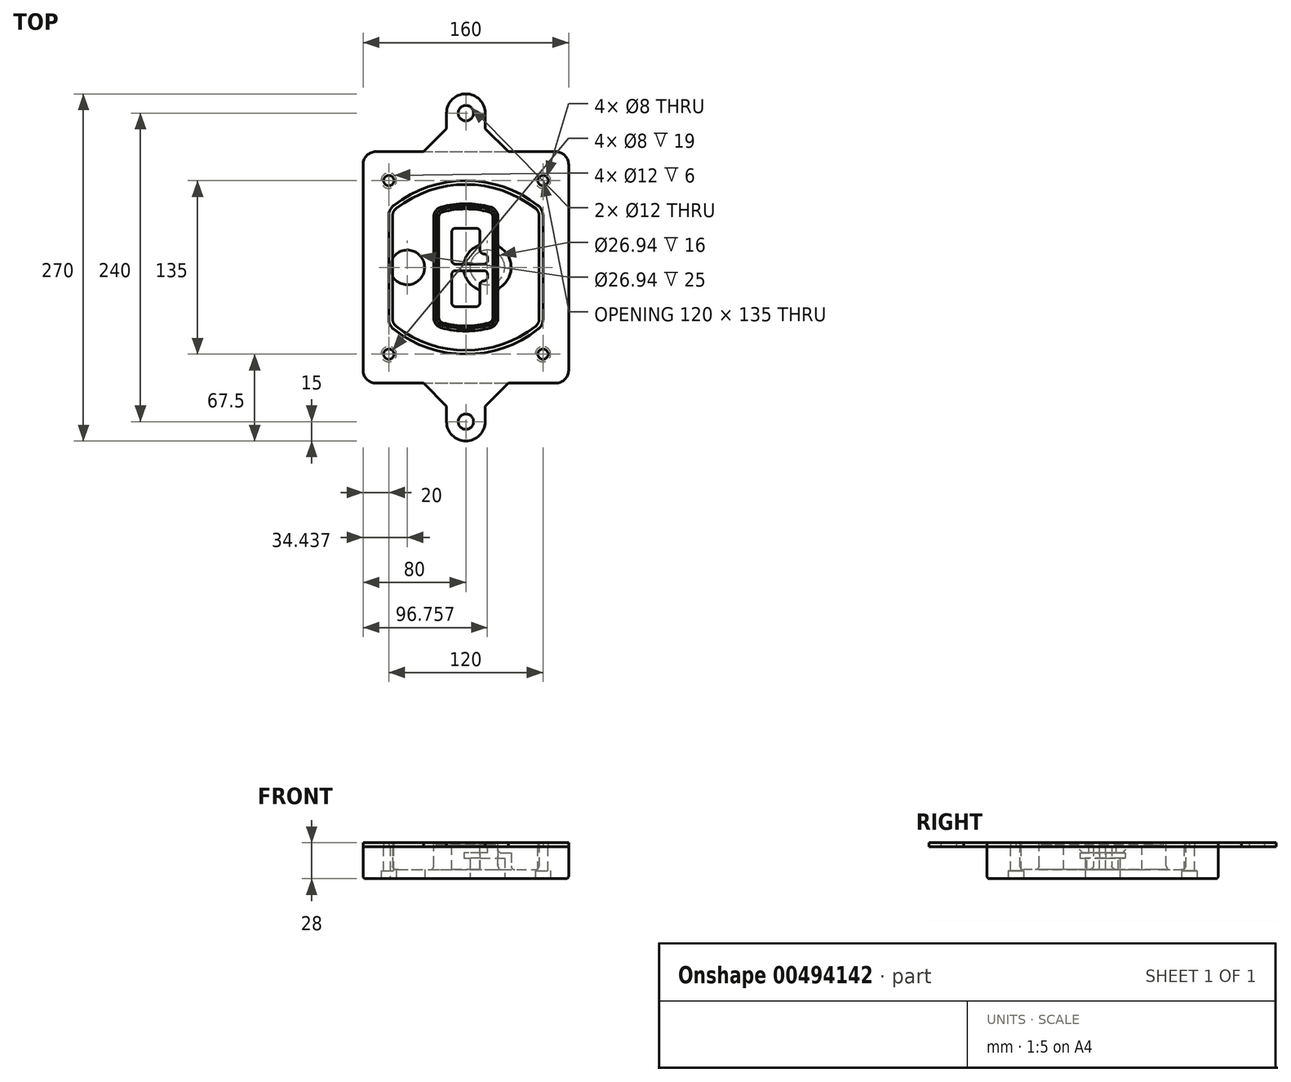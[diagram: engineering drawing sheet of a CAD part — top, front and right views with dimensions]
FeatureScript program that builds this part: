
annotation { "Feature Type Name" : "Feature", "Feature Type Description" : "" }
export const myFeature = defineFeature(function(context is Context, id is Id, definition is map)
    precondition{}
    {
        {
            var Q0;
            Q0=qCreatedBy(makeId("Top.planeOp"),FACE);
            var sketch = newSketch(context, id + "F0", { "sketchPlane" : qUnion([Q0])});
            skPoint(sketch, "E0.rect.middle", {"position": v(0, 0) * mm});
            skLineSegment(sketch, "E1.bottom", {"start": v(-70, -90) * mm, "end": v(70, -90) * mm});
            skLineSegment(sketch, "E1.top", {"start": v(-70, 90) * mm, "end": v(70, 90) * mm});
            skLineSegment(sketch, "E1.left", {"start": v(-80, -80) * mm, "end": v(-80, 80) * mm});
            skLineSegment(sketch, "E1.right", {"start": v(80, -80) * mm, "end": v(80, 80) * mm});
            skLineSegment(sketch, "E2", {"start": v(-80, 90) * mm, "end": v(80, -90) * mm, "construction": true});
            skLineSegment(sketch, "E3", {"start": v(80, 90) * mm, "end": v(-80, -90) * mm, "construction": true});
            skCircle(sketch, "E4", {"center": v(-60, 67.5) * mm, "radius": 4 * mm});
            skCircle(sketch, "E5", {"center": v(60, 67.5) * mm, "radius": 4 * mm});
            skCircle(sketch, "E6", {"center": v(60, -67.5) * mm, "radius": 4 * mm});
            skCircle(sketch, "E7", {"center": v(-60, -67.5) * mm, "radius": 4 * mm});
            skLineSegment(sketch, "E8", {"start": v(-60, 67.5) * mm, "end": v(60, 67.5) * mm, "construction": true});
            skLineSegment(sketch, "E9", {"start": v(60, 67.5) * mm, "end": v(60, -67.5) * mm, "construction": true});
            skLineSegment(sketch, "E10", {"start": v(60, -67.5) * mm, "end": v(-60, -67.5) * mm, "construction": true});
            skLineSegment(sketch, "E11", {"start": v(-60, -67.5) * mm, "end": v(-60, 67.5) * mm, "construction": true});
            skLineSegment(sketch, "E12", {"start": v(-60, 40.3) * mm, "end": v(-60, -40.3) * mm});
            skLineSegment(sketch, "E13", {"start": v(60, 40.3) * mm, "end": v(60, -40.3) * mm});
            skArc(sketch, "E14", {"start": v(56.15, 48.18) * mm, "mid": v(0, 67.5) * mm, "end": v(-56.15, 48.18) * mm});
            skArc(sketch, "E15", {"start": v(-56.15, -48.18) * mm, "mid": v(0, -67.5) * mm, "end": v(56.15, -48.18) * mm});
            skLineSegment(sketch, "E16", {"start": v(-60, 0) * mm, "end": v(60, 0) * mm, "construction": true});
            skPoint(sketch, "E17.visualSharp", {"position": v(-60, -45) * mm});
            skArc(sketch, "E17.filletArc", {"start": v(-60, -40.3) * mm, "mid": v(-58.99, -44.68) * mm, "end": v(-56.15, -48.18) * mm});
            skPoint(sketch, "E18.visualSharp", {"position": v(-60, 45) * mm});
            skArc(sketch, "E18.filletArc", {"start": v(-56.15, 48.18) * mm, "mid": v(-58.99, 44.68) * mm, "end": v(-60, 40.3) * mm});
            skPoint(sketch, "E19.visualSharp", {"position": v(60, 45) * mm});
            skArc(sketch, "E19.filletArc", {"start": v(60, 40.3) * mm, "mid": v(58.99, 44.68) * mm, "end": v(56.15, 48.18) * mm});
            skPoint(sketch, "E20.visualSharp", {"position": v(60, -45) * mm});
            skArc(sketch, "E20.filletArc", {"start": v(56.15, -48.18) * mm, "mid": v(58.99, -44.68) * mm, "end": v(60, -40.3) * mm});
            skPoint(sketch, "E21.visualSharp", {"position": v(-80, 90) * mm});
            skArc(sketch, "E21.filletArc", {"start": v(-70, 90) * mm, "mid": v(-77.07, 87.07) * mm, "end": v(-80, 80) * mm});
            skPoint(sketch, "E22.visualSharp", {"position": v(80, 90) * mm});
            skArc(sketch, "E22.filletArc", {"start": v(80, 80) * mm, "mid": v(77.07, 87.07) * mm, "end": v(70, 90) * mm});
            skPoint(sketch, "E23.visualSharp", {"position": v(80, -90) * mm});
            skArc(sketch, "E23.filletArc", {"start": v(70, -90) * mm, "mid": v(77.07, -87.07) * mm, "end": v(80, -80) * mm});
            skPoint(sketch, "E24.visualSharp", {"position": v(-80, -90) * mm});
            skArc(sketch, "E24.filletArc", {"start": v(-80, -80) * mm, "mid": v(-77.07, -87.07) * mm, "end": v(-70, -90) * mm});
            skArc(sketch, "E25.0", {"start": v(57, 40.3) * mm, "mid": v(56.3, 43.36) * mm, "end": v(54.3, 45.81) * mm});
            skLineSegment(sketch, "E25.1", {"start": v(57, 40.3) * mm, "end": v(57, -40.3) * mm});
            skArc(sketch, "E25.2", {"start": v(54.3, -45.81) * mm, "mid": v(56.3, -43.36) * mm, "end": v(57, -40.3) * mm});
            skArc(sketch, "E25.3", {"start": v(-54.3, -45.81) * mm, "mid": v(0, -64.5) * mm, "end": v(54.3, -45.81) * mm});
            skArc(sketch, "E25.4", {"start": v(-57, -40.3) * mm, "mid": v(-56.3, -43.36) * mm, "end": v(-54.3, -45.81) * mm});
            skArc(sketch, "E25.5", {"start": v(54.3, 45.81) * mm, "mid": v(0, 64.5) * mm, "end": v(-54.3, 45.81) * mm});
            skLineSegment(sketch, "E25.6", {"start": v(-57, 40.3) * mm, "end": v(-57, -40.3) * mm});
            skArc(sketch, "E25.7", {"start": v(-54.3, 45.81) * mm, "mid": v(-56.3, 43.36) * mm, "end": v(-57, 40.3) * mm});
            skArc(sketch, "E26.0", {"start": v(-58.62, 51.33) * mm, "mid": v(-62.58, 46.43) * mm, "end": v(-64, 40.3) * mm});
            skArc(sketch, "E26.1", {"start": v(58.62, 51.33) * mm, "mid": v(0, 71.5) * mm, "end": v(-58.62, 51.33) * mm});
            skArc(sketch, "E26.2", {"start": v(64, 40.3) * mm, "mid": v(62.58, 46.43) * mm, "end": v(58.62, 51.33) * mm});
            skLineSegment(sketch, "E26.3", {"start": v(64, 40.3) * mm, "end": v(64, -40.3) * mm});
            skArc(sketch, "E26.4", {"start": v(58.62, -51.33) * mm, "mid": v(62.58, -46.43) * mm, "end": v(64, -40.3) * mm});
            skLineSegment(sketch, "E26.5", {"start": v(-64, 40.3) * mm, "end": v(-64, -40.3) * mm});
            skArc(sketch, "E26.6", {"start": v(-58.62, -51.33) * mm, "mid": v(0, -71.5) * mm, "end": v(58.62, -51.33) * mm});
            skArc(sketch, "E26.7", {"start": v(-64, -40.3) * mm, "mid": v(-62.58, -46.43) * mm, "end": v(-58.62, -51.33) * mm});
            skSolve(sketch);
        }
        {
            var Q0;
            Q0=makeQuery(id+"F0.imprint","IMPRINT",FACE,{"disambiguationData":[TD([[makeQuery(id+"F0.imprint","IMPRINT",EDGE,{"derivedFrom":sQuery(id+"F0.wireOp",EDGE,"E1.bottom")}),1.0]])]});
            var Q1;
            Q1=makeQuery(id+"F0.imprint","IMPRINT",FACE,{"disambiguationData":[TD([[makeQuery(id+"F0.imprint","IMPRINT",EDGE,{"derivedFrom":sQuery(id+"F0.wireOp",EDGE,"E12")}),1.0]])]});
            var Q2;
            Q2=makeQuery(id+"F0.imprint","IMPRINT",FACE,{"disambiguationData":[TD([[makeQuery(id+"F0.imprint","IMPRINT",EDGE,{"derivedFrom":sQuery(id+"F0.wireOp",EDGE,"E25.0")}),1.0]])]});
            var Q3;
            Q3=makeQuery(id+"F0.imprint","IMPRINT",FACE,{"disambiguationData":[TD([[makeQuery(id+"F0.imprint","IMPRINT",EDGE,{"derivedFrom":sQuery(id+"F0.wireOp",EDGE,"E12")}),-1.0]])]});
            extrude(context, id + "F1", {"entities" : qUnion([Q0, Q1, Q2, Q3]), "oppositeDirection" : true, "depth" : 25 * mm});
        }
        {
            var Q0;
            Q0=makeQuery(id+"F0.imprint","IMPRINT",FACE,{"disambiguationData":[TD([[makeQuery(id+"F0.imprint","IMPRINT",EDGE,{"derivedFrom":sQuery(id+"F0.wireOp",EDGE,"E12")}),1.0]])]});
            extrude(context, id + "F2", {"entities" : qUnion([Q0]), "operationType" : NewBodyOperationType.ADD, "depth" : 3 * mm});
        }
        {
            var Q0;
            Q0=makeQuery(id+"F0.imprint","IMPRINT",FACE,{"disambiguationData":[TD([[makeQuery(id+"F0.imprint","IMPRINT",EDGE,{"derivedFrom":sQuery(id+"F0.wireOp",EDGE,"E25.0")}),1.0]])]});
            extrude(context, id + "F3", {"entities" : qUnion([Q0]), "operationType" : NewBodyOperationType.REMOVE, "oppositeDirection" : true, "depth" : 18 * mm});
        }
        {
            var Q0;
            Q0=makeQuery(id+"F2.opExtrude","CAP_FACE",FACE,{"disambiguationData":[OSD([sQuery(id+"F0.wireOp",EDGE,"E12"),sQuery(id+"F0.wireOp",EDGE,"E13"),sQuery(id+"F0.wireOp",EDGE,"E14"),sQuery(id+"F0.wireOp",EDGE,"E15"),sQuery(id+"F0.wireOp",EDGE,"E17.filletArc"),sQuery(id+"F0.wireOp",EDGE,"E18.filletArc"),sQuery(id+"F0.wireOp",EDGE,"E19.filletArc"),sQuery(id+"F0.wireOp",EDGE,"E20.filletArc"),sQuery(id+"F0.wireOp",EDGE,"E25.0"),sQuery(id+"F0.wireOp",EDGE,"E25.1"),sQuery(id+"F0.wireOp",EDGE,"E25.2"),sQuery(id+"F0.wireOp",EDGE,"E25.3"),sQuery(id+"F0.wireOp",EDGE,"E25.4"),sQuery(id+"F0.wireOp",EDGE,"E25.5"),sQuery(id+"F0.wireOp",EDGE,"E25.6"),sQuery(id+"F0.wireOp",EDGE,"E25.7")])],"isStart":false});
            var sketch = newSketch(context, id + "F4", { "sketchPlane" : qUnion([Q0])});
            skArc(sketch, "E27.0", {"start": v(-19.08, -46.97) * mm, "mid": v(0, -49.5) * mm, "end": v(19.08, -46.97) * mm});
            skArc(sketch, "E28.0", {"start": v(19.08, 46.97) * mm, "mid": v(0, 49.5) * mm, "end": v(-19.08, 46.97) * mm});
            skLineSegment(sketch, "E29", {"start": v(-25, 39.25) * mm, "end": v(-25, -39.25) * mm});
            skLineSegment(sketch, "E30", {"start": v(25, 39.25) * mm, "end": v(25, -39.25) * mm});
            skLineSegment(sketch, "E31", {"start": v(-25, 45.1) * mm, "end": v(25, 45.1) * mm, "construction": true});
            skLineSegment(sketch, "E32", {"start": v(-25, -45.1) * mm, "end": v(25, -45.1) * mm, "construction": true});
            skPoint(sketch, "E33.visualSharp", {"position": v(-25, 45.1) * mm});
            skArc(sketch, "E33.filletArc", {"start": v(-19.08, 46.97) * mm, "mid": v(-23.35, 44.11) * mm, "end": v(-25, 39.25) * mm});
            skPoint(sketch, "E34.visualSharp", {"position": v(25, 45.1) * mm});
            skArc(sketch, "E34.filletArc", {"start": v(25, 39.25) * mm, "mid": v(23.35, 44.11) * mm, "end": v(19.08, 46.97) * mm});
            skPoint(sketch, "E35.visualSharp", {"position": v(25, -45.1) * mm});
            skArc(sketch, "E35.filletArc", {"start": v(19.08, -46.97) * mm, "mid": v(23.35, -44.11) * mm, "end": v(25, -39.25) * mm});
            skPoint(sketch, "E36.visualSharp", {"position": v(-25, -45.1) * mm});
            skArc(sketch, "E36.filletArc", {"start": v(-25, -39.25) * mm, "mid": v(-23.35, -44.11) * mm, "end": v(-19.08, -46.97) * mm});
            skArc(sketch, "E37.0", {"start": v(54.3, 45.81) * mm, "mid": v(0, 64.5) * mm, "end": v(-54.3, 45.81) * mm});
            skArc(sketch, "E37.1", {"start": v(-54.3, 45.81) * mm, "mid": v(-56.3, 43.36) * mm, "end": v(-57, 40.3) * mm});
            skLineSegment(sketch, "E37.2", {"start": v(-57, 40.3) * mm, "end": v(-57, -40.3) * mm});
            skArc(sketch, "E37.3", {"start": v(-57, -40.3) * mm, "mid": v(-56.3, -43.36) * mm, "end": v(-54.3, -45.81) * mm});
            skArc(sketch, "E37.4", {"start": v(-54.3, -45.81) * mm, "mid": v(0, -64.5) * mm, "end": v(54.3, -45.81) * mm});
            skArc(sketch, "E37.5", {"start": v(54.3, -45.81) * mm, "mid": v(56.3, -43.36) * mm, "end": v(57, -40.3) * mm});
            skLineSegment(sketch, "E37.6", {"start": v(57, 40.3) * mm, "end": v(57, -40.3) * mm});
            skArc(sketch, "E37.7", {"start": v(57, 40.3) * mm, "mid": v(56.3, 43.36) * mm, "end": v(54.3, 45.81) * mm});
            skLineSegment(sketch, "E38.0", {"start": v(23, 39.25) * mm, "end": v(23, -39.25) * mm});
            skArc(sketch, "E38.1", {"start": v(18.56, -45.04) * mm, "mid": v(21.76, -42.9) * mm, "end": v(23, -39.25) * mm});
            skArc(sketch, "E38.2", {"start": v(-18.56, -45.04) * mm, "mid": v(0, -47.5) * mm, "end": v(18.56, -45.04) * mm});
            skArc(sketch, "E38.3", {"start": v(-23, -39.25) * mm, "mid": v(-21.76, -42.9) * mm, "end": v(-18.56, -45.04) * mm});
            skLineSegment(sketch, "E38.4", {"start": v(-23, 39.25) * mm, "end": v(-23, -39.25) * mm});
            skArc(sketch, "E38.5", {"start": v(23, 39.25) * mm, "mid": v(21.76, 42.9) * mm, "end": v(18.56, 45.04) * mm});
            skArc(sketch, "E38.6", {"start": v(-18.56, 45.04) * mm, "mid": v(-21.76, 42.9) * mm, "end": v(-23, 39.25) * mm});
            skArc(sketch, "E38.7", {"start": v(18.56, 45.04) * mm, "mid": v(0, 47.5) * mm, "end": v(-18.56, 45.04) * mm});
            skArc(sketch, "E39.0", {"start": v(21, 39.25) * mm, "mid": v(20.18, 41.68) * mm, "end": v(18.04, 43.1) * mm});
            skLineSegment(sketch, "E39.1", {"start": v(21, 39.25) * mm, "end": v(21, -39.25) * mm});
            skArc(sketch, "E39.2", {"start": v(18.04, -43.1) * mm, "mid": v(20.18, -41.68) * mm, "end": v(21, -39.25) * mm});
            skArc(sketch, "E39.3", {"start": v(-18.04, -43.1) * mm, "mid": v(0, -45.5) * mm, "end": v(18.04, -43.1) * mm});
            skArc(sketch, "E39.4", {"start": v(-21, -39.25) * mm, "mid": v(-20.18, -41.68) * mm, "end": v(-18.04, -43.1) * mm});
            skArc(sketch, "E39.5", {"start": v(18.04, 43.1) * mm, "mid": v(0, 45.5) * mm, "end": v(-18.04, 43.1) * mm});
            skLineSegment(sketch, "E39.6", {"start": v(-21, 39.25) * mm, "end": v(-21, -39.25) * mm});
            skArc(sketch, "E39.7", {"start": v(-18.04, 43.1) * mm, "mid": v(-20.18, 41.68) * mm, "end": v(-21, 39.25) * mm});
            skLineSegment(sketch, "E40", {"start": v(-25, 0) * mm, "end": v(25, 0) * mm, "construction": true});
            skLineSegment(sketch, "E41", {"start": v(-11, 5.5) * mm, "end": v(-11, 27.5) * mm});
            skLineSegment(sketch, "E42", {"start": v(-8, 30.5) * mm, "end": v(8, 30.5) * mm});
            skLineSegment(sketch, "E43", {"start": v(11, 27.5) * mm, "end": v(11, 13.5) * mm});
            skLineSegment(sketch, "E44", {"start": v(14, 10.5) * mm, "end": v(14, 10.5) * mm});
            skLineSegment(sketch, "E45", {"start": v(17, 7.5) * mm, "end": v(17, 5.5) * mm});
            skLineSegment(sketch, "E46", {"start": v(14, 2.5) * mm, "end": v(-8, 2.5) * mm});
            skPoint(sketch, "E47.visualSharp", {"position": v(-11, 30.5) * mm});
            skArc(sketch, "E47.filletArc", {"start": v(-8, 30.5) * mm, "mid": v(-10.12, 29.62) * mm, "end": v(-11, 27.5) * mm});
            skPoint(sketch, "E48.visualSharp", {"position": v(11, 30.5) * mm});
            skArc(sketch, "E48.filletArc", {"start": v(11, 27.5) * mm, "mid": v(10.12, 29.62) * mm, "end": v(8, 30.5) * mm});
            skPoint(sketch, "E49.visualSharp", {"position": v(11, 10.5) * mm});
            skArc(sketch, "E49.filletArc", {"start": v(11, 13.5) * mm, "mid": v(11.88, 11.38) * mm, "end": v(14, 10.5) * mm});
            skPoint(sketch, "E50.visualSharp", {"position": v(17, 10.5) * mm});
            skArc(sketch, "E50.filletArc", {"start": v(17, 7.5) * mm, "mid": v(16.12, 9.62) * mm, "end": v(14, 10.5) * mm});
            skPoint(sketch, "E51.visualSharp", {"position": v(17, 2.5) * mm});
            skArc(sketch, "E51.filletArc", {"start": v(14, 2.5) * mm, "mid": v(16.12, 3.38) * mm, "end": v(17, 5.5) * mm});
            skPoint(sketch, "E52.visualSharp", {"position": v(-11, 2.5) * mm});
            skArc(sketch, "E52.filletArc", {"start": v(-11, 5.5) * mm, "mid": v(-10.12, 3.38) * mm, "end": v(-8, 2.5) * mm});
            skLineSegment(sketch, "E53.0.MirrorCS", {"start": v(14, -2.5) * mm, "end": v(-8, -2.5) * mm});
            skArc(sketch, "E54.0.MirrorCS", {"start": v(-11, -5.5) * mm, "mid": v(-10.12, -3.38) * mm, "end": v(-8, -2.5) * mm});
            skLineSegment(sketch, "E55.0.MirrorCS", {"start": v(-11, -5.5) * mm, "end": v(-11, -27.5) * mm});
            skArc(sketch, "E56.0.MirrorCS", {"start": v(-8, -30.5) * mm, "mid": v(-10.12, -29.62) * mm, "end": v(-11, -27.5) * mm});
            skLineSegment(sketch, "E57.0.MirrorCS", {"start": v(-8, -30.5) * mm, "end": v(8, -30.5) * mm});
            skArc(sketch, "E58.0.MirrorCS", {"start": v(11, -27.5) * mm, "mid": v(10.12, -29.62) * mm, "end": v(8, -30.5) * mm});
            skLineSegment(sketch, "E59.0.MirrorCS", {"start": v(11, -27.5) * mm, "end": v(11, -13.5) * mm});
            skArc(sketch, "E60.0.MirrorCS", {"start": v(11, -13.5) * mm, "mid": v(11.88, -11.38) * mm, "end": v(14, -10.5) * mm});
            skArc(sketch, "E61.0.MirrorCS", {"start": v(17, -7.5) * mm, "mid": v(16.12, -9.62) * mm, "end": v(14, -10.5) * mm});
            skLineSegment(sketch, "E62.0.MirrorCS", {"start": v(17, -7.5) * mm, "end": v(17, -5.5) * mm});
            skArc(sketch, "E63.0.MirrorCS", {"start": v(14, -2.5) * mm, "mid": v(16.12, -3.38) * mm, "end": v(17, -5.5) * mm});
            skSolve(sketch);
        }
        {
            var Q0;
            Q0=makeQuery(id+"F4.imprint","IMPRINT",FACE,{"disambiguationData":[TD([[makeQuery(id+"F4.imprint","IMPRINT",EDGE,{"derivedFrom":sQuery(id+"F4.wireOp",EDGE,"E27.0")}),1.0]])]});
            var Q1;
            Q1=makeQuery(id+"F4.imprint","IMPRINT",FACE,{"disambiguationData":[TD([[makeQuery(id+"F4.imprint","IMPRINT",EDGE,{"derivedFrom":sQuery(id+"F4.wireOp",EDGE,"E38.0")}),-1.0]])]});
            var Q2;
            Q2=makeQuery(id+"F4.imprint","IMPRINT",FACE,{"disambiguationData":[TD([[makeQuery(id+"F4.imprint","IMPRINT",EDGE,{"derivedFrom":sQuery(id+"F4.wireOp",EDGE,"E39.0")}),1.0]])]});
            extrude(context, id + "F5", {"entities" : qUnion([Q0, Q1, Q2]), "operationType" : NewBodyOperationType.ADD, "endBound" : BoundingType.UP_TO_NEXT, "oppositeDirection" : true, "depth" : 25 * mm});
        }
        {
            var Q0;
            Q0=makeQuery(id+"F4.imprint","IMPRINT",FACE,{"disambiguationData":[TD([[makeQuery(id+"F4.imprint","IMPRINT",EDGE,{"derivedFrom":sQuery(id+"F4.wireOp",EDGE,"E38.0")}),-1.0]])]});
            extrude(context, id + "F6", {"entities" : qUnion([Q0]), "operationType" : NewBodyOperationType.REMOVE, "oppositeDirection" : true, "depth" : 2 * mm});
        }
        {
            var Q0;
            Q0=makeQuery(id+"F1.opExtrude","CAP_FACE",FACE,{"disambiguationData":[OSD([sQuery(id+"F0.wireOp",EDGE,"E1.bottom"),sQuery(id+"F0.wireOp",EDGE,"E1.top"),sQuery(id+"F0.wireOp",EDGE,"E1.left"),sQuery(id+"F0.wireOp",EDGE,"E1.right"),sQuery(id+"F0.wireOp",EDGE,"E4"),sQuery(id+"F0.wireOp",EDGE,"E5"),sQuery(id+"F0.wireOp",EDGE,"E6"),sQuery(id+"F0.wireOp",EDGE,"E7"),sQuery(id+"F0.wireOp",EDGE,"E21.filletArc"),sQuery(id+"F0.wireOp",EDGE,"E22.filletArc"),sQuery(id+"F0.wireOp",EDGE,"E23.filletArc"),sQuery(id+"F0.wireOp",EDGE,"E24.filletArc")])],"isStart":false});
            var sketch = newSketch(context, id + "F7", { "sketchPlane" : qUnion([Q0])});
            skCircle(sketch, "E64", {"center": v(16.76, 0) * mm, "radius": 13.47 * mm});
            skCircle(sketch, "E65", {"center": v(-45.56, 0) * mm, "radius": 13.47 * mm});
            skLineSegment(sketch, "E66", {"start": v(80, 0) * mm, "end": v(-80, 0) * mm});
            skCircle(sketch, "E67", {"center": v(16.76, 0) * mm, "radius": 18.47 * mm});
            skCircle(sketch, "E68", {"center": v(60, -67.5) * mm, "radius": 6 * mm});
            skCircle(sketch, "E69", {"center": v(-60, -67.5) * mm, "radius": 6 * mm});
            skCircle(sketch, "E70", {"center": v(-60, 67.5) * mm, "radius": 6 * mm});
            skCircle(sketch, "E71", {"center": v(60, 67.5) * mm, "radius": 6 * mm});
            skSolve(sketch);
        }
        {
            var Q0;
            {var subQ1=sQuery(id+"F7.wireOp",EDGE,"E66");var subQ4=sQuery(id+"F7.wireOp",EDGE,"E64");var subQ6=makeQuery(id+"F7.imprint","INTERSECT",VERTEX,{"disambiguationData":[OD(0.0)],"derivedFrom":[subQ4,subQ1]});Q0=makeQuery(id+"F7.imprint","IMPRINT",FACE,{"disambiguationData":[TD([[makeQuery(id+"F7.imprint","IMPRINT",EDGE,{"disambiguationData":[TD([[subQ6,-1.0]])],"derivedFrom":subQ4}),-1.0]])]});}
            var Q1;
            {var subQ0=sQuery(id+"F7.wireOp",EDGE,"E66");var subQ1=sQuery(id+"F7.wireOp",EDGE,"E64");var subQ3=makeQuery(id+"F7.imprint","INTERSECT",VERTEX,{"disambiguationData":[OD(0.0)],"derivedFrom":[subQ1,subQ0]});Q1=makeQuery(id+"F7.imprint","IMPRINT",FACE,{"disambiguationData":[TD([[makeQuery(id+"F7.imprint","IMPRINT",EDGE,{"disambiguationData":[TD([[subQ3,-1.0]])],"derivedFrom":subQ1}),1.0]])]});}
            var Q2;
            {var subQ0=sQuery(id+"F7.wireOp",EDGE,"E66");var subQ1=sQuery(id+"F7.wireOp",EDGE,"E64");var subQ3=makeQuery(id+"F7.imprint","INTERSECT",VERTEX,{"disambiguationData":[OD(0.0)],"derivedFrom":[subQ1,subQ0]});Q2=makeQuery(id+"F7.imprint","IMPRINT",FACE,{"disambiguationData":[TD([[makeQuery(id+"F7.imprint","IMPRINT",EDGE,{"disambiguationData":[TD([[subQ3,1.0]])],"derivedFrom":subQ1}),1.0]])]});}
            var Q3;
            {var subQ1=sQuery(id+"F7.wireOp",EDGE,"E66");var subQ4=sQuery(id+"F7.wireOp",EDGE,"E64");var subQ6=makeQuery(id+"F7.imprint","INTERSECT",VERTEX,{"disambiguationData":[OD(0.0)],"derivedFrom":[subQ4,subQ1]});Q3=makeQuery(id+"F7.imprint","IMPRINT",FACE,{"disambiguationData":[TD([[makeQuery(id+"F7.imprint","IMPRINT",EDGE,{"disambiguationData":[TD([[subQ6,1.0]])],"derivedFrom":subQ4}),-1.0]])]});}
            extrude(context, id + "F8", {"entities" : qUnion([Q0, Q1, Q2, Q3]), "operationType" : NewBodyOperationType.ADD, "oppositeDirection" : true, "depth" : 20 * mm});
        }
        {
            var Q0;
            {var subQ0=sQuery(id+"F7.wireOp",EDGE,"E66");var subQ1=sQuery(id+"F7.wireOp",EDGE,"E64");var subQ3=makeQuery(id+"F7.imprint","INTERSECT",VERTEX,{"disambiguationData":[OD(0.0)],"derivedFrom":[subQ1,subQ0]});Q0=makeQuery(id+"F7.imprint","IMPRINT",FACE,{"disambiguationData":[TD([[makeQuery(id+"F7.imprint","IMPRINT",EDGE,{"disambiguationData":[TD([[subQ3,-1.0]])],"derivedFrom":subQ1}),1.0]])]});}
            var Q1;
            {var subQ0=sQuery(id+"F7.wireOp",EDGE,"E66");var subQ1=sQuery(id+"F7.wireOp",EDGE,"E64");var subQ3=makeQuery(id+"F7.imprint","INTERSECT",VERTEX,{"disambiguationData":[OD(0.0)],"derivedFrom":[subQ1,subQ0]});Q1=makeQuery(id+"F7.imprint","IMPRINT",FACE,{"disambiguationData":[TD([[makeQuery(id+"F7.imprint","IMPRINT",EDGE,{"disambiguationData":[TD([[subQ3,1.0]])],"derivedFrom":subQ1}),1.0]])]});}
            extrude(context, id + "F9", {"entities" : qUnion([Q0, Q1]), "operationType" : NewBodyOperationType.REMOVE, "oppositeDirection" : true, "depth" : 16 * mm});
        }
        {
            var Q0;
            {var subQ0=sQuery(id+"F7.wireOp",EDGE,"E66");var subQ1=sQuery(id+"F7.wireOp",EDGE,"E65");var subQ3=makeQuery(id+"F7.imprint","INTERSECT",VERTEX,{"disambiguationData":[OD(0.0)],"derivedFrom":[subQ1,subQ0]});Q0=makeQuery(id+"F7.imprint","IMPRINT",FACE,{"disambiguationData":[TD([[makeQuery(id+"F7.imprint","IMPRINT",EDGE,{"disambiguationData":[TD([[subQ3,-1.0]])],"derivedFrom":subQ1}),1.0]])]});}
            var Q1;
            {var subQ0=sQuery(id+"F7.wireOp",EDGE,"E66");var subQ1=sQuery(id+"F7.wireOp",EDGE,"E65");var subQ3=makeQuery(id+"F7.imprint","INTERSECT",VERTEX,{"disambiguationData":[OD(0.0)],"derivedFrom":[subQ1,subQ0]});Q1=makeQuery(id+"F7.imprint","IMPRINT",FACE,{"disambiguationData":[TD([[makeQuery(id+"F7.imprint","IMPRINT",EDGE,{"disambiguationData":[TD([[subQ3,1.0]])],"derivedFrom":subQ1}),1.0]])]});}
            extrude(context, id + "F10", {"entities" : qUnion([Q0, Q1]), "operationType" : NewBodyOperationType.REMOVE, "oppositeDirection" : true, "depth" : 25 * mm});
        }
        {
            var Q0;
            Q0=makeQuery(id+"F7.imprint","IMPRINT",FACE,{"disambiguationData":[TD([[makeQuery(id+"F7.imprint","IMPRINT",EDGE,{"derivedFrom":sQuery(id+"F7.wireOp",EDGE,"E68")}),1.0]])]});
            var Q1;
            Q1=makeQuery(id+"F7.imprint","IMPRINT",FACE,{"disambiguationData":[TD([[makeQuery(id+"F7.imprint","IMPRINT",EDGE,{"derivedFrom":makeQuery(id+"F1.opExtrude","CAP_EDGE",EDGE,{"disambiguationData":[OSD([sQuery(id+"F0.wireOp",EDGE,"E5")])],"isStart":false})}),-1.0]])]});
            var Q2;
            Q2=makeQuery(id+"F7.imprint","IMPRINT",FACE,{"disambiguationData":[TD([[makeQuery(id+"F7.imprint","IMPRINT",EDGE,{"derivedFrom":sQuery(id+"F7.wireOp",EDGE,"E69")}),1.0]])]});
            var Q3;
            Q3=makeQuery(id+"F7.imprint","IMPRINT",FACE,{"disambiguationData":[TD([[makeQuery(id+"F7.imprint","IMPRINT",EDGE,{"derivedFrom":makeQuery(id+"F1.opExtrude","CAP_EDGE",EDGE,{"disambiguationData":[OSD([sQuery(id+"F0.wireOp",EDGE,"E4")])],"isStart":false})}),-1.0]])]});
            var Q4;
            Q4=makeQuery(id+"F7.imprint","IMPRINT",FACE,{"disambiguationData":[TD([[makeQuery(id+"F7.imprint","IMPRINT",EDGE,{"derivedFrom":sQuery(id+"F7.wireOp",EDGE,"E70")}),1.0]])]});
            var Q5;
            Q5=makeQuery(id+"F7.imprint","IMPRINT",FACE,{"disambiguationData":[TD([[makeQuery(id+"F7.imprint","IMPRINT",EDGE,{"derivedFrom":makeQuery(id+"F1.opExtrude","CAP_EDGE",EDGE,{"disambiguationData":[OSD([sQuery(id+"F0.wireOp",EDGE,"E7")])],"isStart":false})}),-1.0]])]});
            var Q6;
            Q6=makeQuery(id+"F7.imprint","IMPRINT",FACE,{"disambiguationData":[TD([[makeQuery(id+"F7.imprint","IMPRINT",EDGE,{"derivedFrom":sQuery(id+"F7.wireOp",EDGE,"E71")}),1.0]])]});
            var Q7;
            Q7=makeQuery(id+"F7.imprint","IMPRINT",FACE,{"disambiguationData":[TD([[makeQuery(id+"F7.imprint","IMPRINT",EDGE,{"derivedFrom":makeQuery(id+"F1.opExtrude","CAP_EDGE",EDGE,{"disambiguationData":[OSD([sQuery(id+"F0.wireOp",EDGE,"E6")])],"isStart":false})}),-1.0]])]});
            extrude(context, id + "F11", {"entities" : qUnion([Q0, Q1, Q2, Q3, Q4, Q5, Q6, Q7]), "operationType" : NewBodyOperationType.REMOVE, "oppositeDirection" : true, "depth" : 6 * mm});
        }
        {
            var Q0;
            Q0=makeQuery(id+"F9.boolean.opBoolean","COPY",FACE,{"derivedFrom":makeQuery(id+"F9.opExtrude","CAP_FACE",FACE,{"disambiguationData":[OSD([sQuery(id+"F7.wireOp",EDGE,"E64")])],"isStart":false})});
            var sketch = newSketch(context, id + "F12", { "sketchPlane" : qUnion([Q0])});
            skArc(sketch, "E72.0", {"start": v(11, 17.55) * mm, "mid": v(2.57, 11.82) * mm, "end": v(-1.54, 2.5) * mm});
            skArc(sketch, "E72.1", {"start": v(-1.54, -2.5) * mm, "mid": v(2.57, -11.82) * mm, "end": v(11, -17.55) * mm});
            skLineSegment(sketch, "E73", {"start": v(-1.54, -2.5) * mm, "end": v(14, -2.5) * mm});
            skLineSegment(sketch, "E74.0", {"start": v(14, 2.5) * mm, "end": v(-1.54, 2.5) * mm});
            skArc(sketch, "E74.1", {"start": v(14, 2.5) * mm, "mid": v(16.12, 3.38) * mm, "end": v(17, 5.5) * mm});
            skLineSegment(sketch, "E74.2", {"start": v(17, 7.5) * mm, "end": v(17, 5.5) * mm});
            skArc(sketch, "E74.3", {"start": v(17, 7.5) * mm, "mid": v(16.12, 9.62) * mm, "end": v(14, 10.5) * mm});
            skArc(sketch, "E74.4", {"start": v(11, 13.5) * mm, "mid": v(11.88, 11.38) * mm, "end": v(14, 10.5) * mm});
            skLineSegment(sketch, "E74.5", {"start": v(11, 17.55) * mm, "end": v(11, 13.5) * mm});
            skLineSegment(sketch, "E74.7", {"start": v(14, -2.5) * mm, "end": v(-1.54, -2.5) * mm});
            skArc(sketch, "E74.8", {"start": v(14, -2.5) * mm, "mid": v(16.12, -3.38) * mm, "end": v(17, -5.5) * mm});
            skLineSegment(sketch, "E74.9", {"start": v(17, -7.5) * mm, "end": v(17, -5.5) * mm});
            skArc(sketch, "E74.10", {"start": v(17, -7.5) * mm, "mid": v(16.12, -9.62) * mm, "end": v(14, -10.5) * mm});
            skArc(sketch, "E74.11", {"start": v(11, -13.5) * mm, "mid": v(11.88, -11.38) * mm, "end": v(14, -10.5) * mm});
            skLineSegment(sketch, "E74.12", {"start": v(11, -17.55) * mm, "end": v(11, -13.5) * mm});
            skPoint(sketch, "E75.orphan", {"position": v(11, -27.5) * mm});
            skPoint(sketch, "E76.orphan", {"position": v(-8, -2.5) * mm});
            skPoint(sketch, "E77.orphan", {"position": v(-8, 2.5) * mm});
            skPoint(sketch, "E78.orphan", {"position": v(11, 27.5) * mm});
            skSolve(sketch);
        }
        {
            var Q0;
            {var subQ7=sQuery(id+"F12.wireOp",EDGE,"E72.0");var subQ14=sQuery(id+"F12.wireOp",EDGE,"E72.1");var subQ16=sQuery(id+"F12.wireOp",EDGE,"E74.1");var subQ18=sQuery(id+"F12.wireOp",EDGE,"E74.8");Q0=qUnion([makeQuery(id+"F12.imprint","IMPRINT",FACE,{"disambiguationData":[TD([[makeQuery(id+"F12.imprint","IMPRINT",EDGE,{"derivedFrom":subQ7}),1.0]])]}),makeQuery(id+"F12.imprint","IMPRINT",FACE,{"disambiguationData":[TD([[makeQuery(id+"F12.imprint","IMPRINT",EDGE,{"derivedFrom":subQ14}),1.0]])]}),makeQuery(id+"F12.imprint","IMPRINT",FACE,{"disambiguationData":[TD([[makeQuery(id+"F12.imprint","IMPRINT",EDGE,{"derivedFrom":subQ16}),1.0]])]}),makeQuery(id+"F12.imprint","IMPRINT",FACE,{"disambiguationData":[TD([[makeQuery(id+"F12.imprint","IMPRINT",EDGE,{"derivedFrom":subQ18}),-1.0]])]})]);}
            var Q1;
            Q1=makeQuery(id+"F5.boolean.opBoolean","SPLIT",FACE,{"disambiguationData":[TD([makeQuery(id+"F5.opExtrude","SWEPT_FACE",FACE,{"disambiguationData":[OSD([sQuery(id+"F4.wireOp",EDGE,"E41")])]})])],"derivedFrom":makeQuery(id+"F3.boolean.opBoolean","COPY",FACE,{"derivedFrom":makeQuery(id+"F3.opExtrude","CAP_FACE",FACE,{"disambiguationData":[OSD([sQuery(id+"F0.wireOp",EDGE,"E25.0"),sQuery(id+"F0.wireOp",EDGE,"E25.1"),sQuery(id+"F0.wireOp",EDGE,"E25.2"),sQuery(id+"F0.wireOp",EDGE,"E25.3"),sQuery(id+"F0.wireOp",EDGE,"E25.4"),sQuery(id+"F0.wireOp",EDGE,"E25.5"),sQuery(id+"F0.wireOp",EDGE,"E25.6"),sQuery(id+"F0.wireOp",EDGE,"E25.7")])],"isStart":false})})});
            extrude(context, id + "F13", {"entities" : qUnion([Q0]), "operationType" : NewBodyOperationType.REMOVE, "endBound" : BoundingType.UP_TO_SURFACE, "endBoundEntityFace" : qUnion([Q1]), "depth" : 25 * mm});
        }
        {
            var Q0;
            Q0=makeQuery(id+"F3.boolean.opBoolean","COPY",EDGE,{"derivedFrom":makeQuery(id+"F3.opExtrude","CAP_EDGE",EDGE,{"disambiguationData":[OSD([sQuery(id+"F0.wireOp",EDGE,"E25.6")])],"isStart":false})});
            var Q1;
            Q1=makeQuery(id+"F8.boolean.opBoolean","INTERSECT",EDGE,{"derivedFrom":[makeQuery(id+"F5.opExtrude","SWEPT_FACE",FACE,{"disambiguationData":[OSD([sQuery(id+"F4.wireOp",EDGE,"E30")])]}),makeQuery(id+"F8.opExtrude","CAP_FACE",FACE,{"disambiguationData":[OSD([sQuery(id+"F7.wireOp",EDGE,"E67")])],"isStart":false})]});
            var Q2;
            Q2=makeQuery(id+"F8.boolean.opBoolean","INTERSECT",EDGE,{"disambiguationData":[OD(1.0)],"derivedFrom":[makeQuery(id+"F5.opExtrude","SWEPT_FACE",FACE,{"disambiguationData":[OSD([sQuery(id+"F4.wireOp",EDGE,"E30")])]}),makeQuery(id+"F8.opExtrude","SWEPT_FACE",FACE,{"disambiguationData":[OSD([sQuery(id+"F7.wireOp",EDGE,"E67")])]})]});
            var Q3;
            {var subQ0=sQuery(id+"F4.wireOp",EDGE,"E30");Q3=makeQuery(id+"F8.boolean.opBoolean","SPLIT",EDGE,{"disambiguationData":[TD([makeQuery(id+"F5.opExtrude","SWEPT_FACE",FACE,{"disambiguationData":[OSD([sQuery(id+"F4.wireOp",EDGE,"E35.filletArc")])]})])],"derivedFrom":makeQuery(id+"F5.opExtrude","CAP_EDGE",EDGE,{"disambiguationData":[OSD([subQ0])],"isStart":false})});}
            var Q4;
            {var subQ0=sQuery(id+"F0.wireOp",EDGE,"E25.7");var subQ1=sQuery(id+"F0.wireOp",EDGE,"E25.1");var subQ2=sQuery(id+"F0.wireOp",EDGE,"E25.6");var subQ3=sQuery(id+"F0.wireOp",EDGE,"E25.5");var subQ4=sQuery(id+"F0.wireOp",EDGE,"E25.4");var subQ5=sQuery(id+"F0.wireOp",EDGE,"E25.0");var subQ6=sQuery(id+"F0.wireOp",EDGE,"E25.2");var subQ7=sQuery(id+"F0.wireOp",EDGE,"E25.3");Q4=makeQuery(id+"F8.boolean.opBoolean","INTERSECT",EDGE,{"derivedFrom":[makeQuery(id+"F5.boolean.opBoolean","SPLIT",FACE,{"disambiguationData":[TD([makeQuery(id+"F2.opExtrude","SWEPT_FACE",FACE,{"disambiguationData":[OSD([subQ5])]})])],"derivedFrom":makeQuery(id+"F3.boolean.opBoolean","COPY",FACE,{"derivedFrom":makeQuery(id+"F3.opExtrude","CAP_FACE",FACE,{"disambiguationData":[OSD([subQ5,subQ1,subQ6,subQ7,subQ4,subQ3,subQ2,subQ0])],"isStart":false})})}),makeQuery(id+"F8.opExtrude","SWEPT_FACE",FACE,{"disambiguationData":[OSD([sQuery(id+"F7.wireOp",EDGE,"E67")])]})]});}
            var Q5;
            Q5=makeQuery(id+"F8.boolean.opBoolean","INTERSECT",EDGE,{"disambiguationData":[OD(0.0)],"derivedFrom":[makeQuery(id+"F5.opExtrude","SWEPT_FACE",FACE,{"disambiguationData":[OSD([sQuery(id+"F4.wireOp",EDGE,"E30")])]}),makeQuery(id+"F8.opExtrude","SWEPT_FACE",FACE,{"disambiguationData":[OSD([sQuery(id+"F7.wireOp",EDGE,"E67")])]})]});
            fillet(context, id + "F14", {"entities" : qUnion([Q0, Q1, Q2, Q3, Q4, Q5]), "radius" : 3 * mm, "tangentPropagation" : true, "allowEdgeOverflow" : false});
        }
        {
            var Q0;
            Q0=makeQuery(id+"F1.opExtrude","CAP_EDGE",EDGE,{"disambiguationData":[OSD([sQuery(id+"F0.wireOp",EDGE,"E1.bottom")])],"isStart":false});
            fillet(context, id + "F15", {"entities" : qUnion([Q0]), "radius" : 2 * mm, "tangentPropagation" : true, "allowEdgeOverflow" : false});
        }
        {
            var Q0;
            {var subQ0=sQuery(id+"F0.wireOp",EDGE,"E21.filletArc");var subQ1=sQuery(id+"F0.wireOp",EDGE,"E7");var subQ2=sQuery(id+"F0.wireOp",EDGE,"E6");var subQ3=sQuery(id+"F0.wireOp",EDGE,"E5");var subQ4=sQuery(id+"F0.wireOp",EDGE,"E4");var subQ5=sQuery(id+"F0.wireOp",EDGE,"E22.filletArc");var subQ6=sQuery(id+"F0.wireOp",EDGE,"E1.bottom");var subQ7=sQuery(id+"F0.wireOp",EDGE,"E1.right");var subQ8=sQuery(id+"F0.wireOp",EDGE,"E1.top");var subQ9=sQuery(id+"F0.wireOp",EDGE,"E1.left");var subQ10=sQuery(id+"F0.wireOp",EDGE,"E23.filletArc");var subQ11=sQuery(id+"F0.wireOp",EDGE,"E24.filletArc");Q0=makeQuery(id+"F2.boolean.opBoolean","SPLIT",FACE,{"disambiguationData":[TD([makeQuery(id+"F1.opExtrude","SWEPT_FACE",FACE,{"disambiguationData":[OSD([subQ6])]})])],"derivedFrom":makeQuery(id+"F1.opExtrude","CAP_FACE",FACE,{"disambiguationData":[OSD([subQ6,subQ8,subQ9,subQ7,subQ4,subQ3,subQ2,subQ1,subQ0,subQ5,subQ10,subQ11])],"isStart":true})});}
            var sketch = newSketch(context, id + "F16", { "sketchPlane" : qUnion([Q0])});
            skLineSegment(sketch, "E79", {"start": v(0, 90) * mm, "end": v(0, 120) * mm, "construction": true});
            skLineSegment(sketch, "E80", {"start": v(-33, 90) * mm, "end": v(-15, 108) * mm});
            skLineSegment(sketch, "E81", {"start": v(-15, 108) * mm, "end": v(-15, 120) * mm});
            skLineSegment(sketch, "E82", {"start": v(33, 90) * mm, "end": v(15, 108) * mm});
            skLineSegment(sketch, "E83", {"start": v(15, 108) * mm, "end": v(15, 120) * mm});
            skArc(sketch, "E84", {"start": v(15, 120) * mm, "mid": v(0, 135) * mm, "end": v(-15, 120) * mm});
            skCircle(sketch, "E85", {"center": v(0, 120) * mm, "radius": 6 * mm});
            skLineSegment(sketch, "E86.0", {"start": v(-70, 90) * mm, "end": v(70, 90) * mm});
            skArc(sketch, "E87.0", {"start": v(-70, 90) * mm, "mid": v(-77.07, 87.07) * mm, "end": v(-80, 80) * mm});
            skArc(sketch, "E88.0", {"start": v(80, 80) * mm, "mid": v(77.07, 87.07) * mm, "end": v(70, 90) * mm});
            skLineSegment(sketch, "E89.0", {"start": v(80, -80) * mm, "end": v(80, 80) * mm});
            skArc(sketch, "E90.0", {"start": v(70, -90) * mm, "mid": v(77.07, -87.07) * mm, "end": v(80, -80) * mm});
            skLineSegment(sketch, "E91.0", {"start": v(-70, -90) * mm, "end": v(70, -90) * mm});
            skArc(sketch, "E92.0", {"start": v(-80, -80) * mm, "mid": v(-77.07, -87.07) * mm, "end": v(-70, -90) * mm});
            skLineSegment(sketch, "E93.0", {"start": v(-80, -80) * mm, "end": v(-80, 80) * mm});
            skArc(sketch, "E94.0", {"start": v(56.15, 48.18) * mm, "mid": v(0, 67.5) * mm, "end": v(-56.15, 48.18) * mm});
            skArc(sketch, "E95.0", {"start": v(60, 40.3) * mm, "mid": v(58.99, 44.68) * mm, "end": v(56.15, 48.18) * mm});
            skLineSegment(sketch, "E96.0", {"start": v(60, 40.3) * mm, "end": v(60, -40.3) * mm});
            skArc(sketch, "E97.0", {"start": v(56.15, -48.18) * mm, "mid": v(58.99, -44.68) * mm, "end": v(60, -40.3) * mm});
            skArc(sketch, "E98.0", {"start": v(-56.15, -48.18) * mm, "mid": v(0, -67.5) * mm, "end": v(56.15, -48.18) * mm});
            skArc(sketch, "E99.0", {"start": v(-60, -40.3) * mm, "mid": v(-58.99, -44.68) * mm, "end": v(-56.15, -48.18) * mm});
            skLineSegment(sketch, "E100.0", {"start": v(-60, 40.3) * mm, "end": v(-60, -40.3) * mm});
            skArc(sketch, "E101.0", {"start": v(-56.15, 48.18) * mm, "mid": v(-58.99, 44.68) * mm, "end": v(-60, 40.3) * mm});
            skCircle(sketch, "E102.0", {"center": v(60, 67.5) * mm, "radius": 4 * mm});
            skCircle(sketch, "E103.0", {"center": v(60, -67.5) * mm, "radius": 4 * mm});
            skCircle(sketch, "E104.0", {"center": v(-60, -67.5) * mm, "radius": 4 * mm});
            skCircle(sketch, "E105.0", {"center": v(-60, 67.5) * mm, "radius": 4 * mm});
            skLineSegment(sketch, "E106", {"start": v(-80, 0) * mm, "end": v(80, 0) * mm, "construction": true});
            skPoint(sketch, "E107.end.orphan", {"position": v(-80, 0) * mm});
            skLineSegment(sketch, "E108.MirrorCS", {"start": v(33, -90) * mm, "end": v(15, -108) * mm});
            skLineSegment(sketch, "E109.MirrorCS", {"start": v(15, -108) * mm, "end": v(15, -120) * mm});
            skArc(sketch, "E110.MirrorCS", {"start": v(15, -120) * mm, "mid": v(0, -135) * mm, "end": v(-15, -120) * mm});
            skCircle(sketch, "E111.MirrorC", {"center": v(0, -120) * mm, "radius": 6 * mm});
            skLineSegment(sketch, "E112.MirrorCS", {"start": v(0, -90) * mm, "end": v(0, -120) * mm, "construction": true});
            skLineSegment(sketch, "E113.MirrorCS", {"start": v(-15, -108) * mm, "end": v(-15, -120) * mm});
            skLineSegment(sketch, "E114.MirrorCS", {"start": v(-33, -90) * mm, "end": v(-15, -108) * mm});
            skSolve(sketch);
        }
        {
            var Q0;
            Q0 = qSketchRegion(id + "F16", true);
            var Q1;
            Q1=makeQuery(id+"F2.opExtrude","CAP_FACE",FACE,{"disambiguationData":[OSD([sQuery(id+"F0.wireOp",EDGE,"E12"),sQuery(id+"F0.wireOp",EDGE,"E13"),sQuery(id+"F0.wireOp",EDGE,"E14"),sQuery(id+"F0.wireOp",EDGE,"E15"),sQuery(id+"F0.wireOp",EDGE,"E17.filletArc"),sQuery(id+"F0.wireOp",EDGE,"E18.filletArc"),sQuery(id+"F0.wireOp",EDGE,"E19.filletArc"),sQuery(id+"F0.wireOp",EDGE,"E20.filletArc"),sQuery(id+"F0.wireOp",EDGE,"E25.0"),sQuery(id+"F0.wireOp",EDGE,"E25.1"),sQuery(id+"F0.wireOp",EDGE,"E25.2"),sQuery(id+"F0.wireOp",EDGE,"E25.3"),sQuery(id+"F0.wireOp",EDGE,"E25.4"),sQuery(id+"F0.wireOp",EDGE,"E25.5"),sQuery(id+"F0.wireOp",EDGE,"E25.6"),sQuery(id+"F0.wireOp",EDGE,"E25.7")])],"isStart":false});
            var Q2;
            Q2=makeQuery(id+"F2.opExtrude","CAP_FACE",FACE,{"disambiguationData":[OSD([sQuery(id+"F0.wireOp",EDGE,"E12"),sQuery(id+"F0.wireOp",EDGE,"E13"),sQuery(id+"F0.wireOp",EDGE,"E14"),sQuery(id+"F0.wireOp",EDGE,"E15"),sQuery(id+"F0.wireOp",EDGE,"E17.filletArc"),sQuery(id+"F0.wireOp",EDGE,"E18.filletArc"),sQuery(id+"F0.wireOp",EDGE,"E19.filletArc"),sQuery(id+"F0.wireOp",EDGE,"E20.filletArc"),sQuery(id+"F0.wireOp",EDGE,"E25.0"),sQuery(id+"F0.wireOp",EDGE,"E25.1"),sQuery(id+"F0.wireOp",EDGE,"E25.2"),sQuery(id+"F0.wireOp",EDGE,"E25.3"),sQuery(id+"F0.wireOp",EDGE,"E25.4"),sQuery(id+"F0.wireOp",EDGE,"E25.5"),sQuery(id+"F0.wireOp",EDGE,"E25.6"),sQuery(id+"F0.wireOp",EDGE,"E25.7")])],"isStart":false});
            extrude(context, id + "F17", {"entities" : qUnion([Q0]), "endBound" : BoundingType.UP_TO_SURFACE, "endBoundEntityFace" : qUnion([Q1]), "depth" : 25 * mm});
        }
    });
